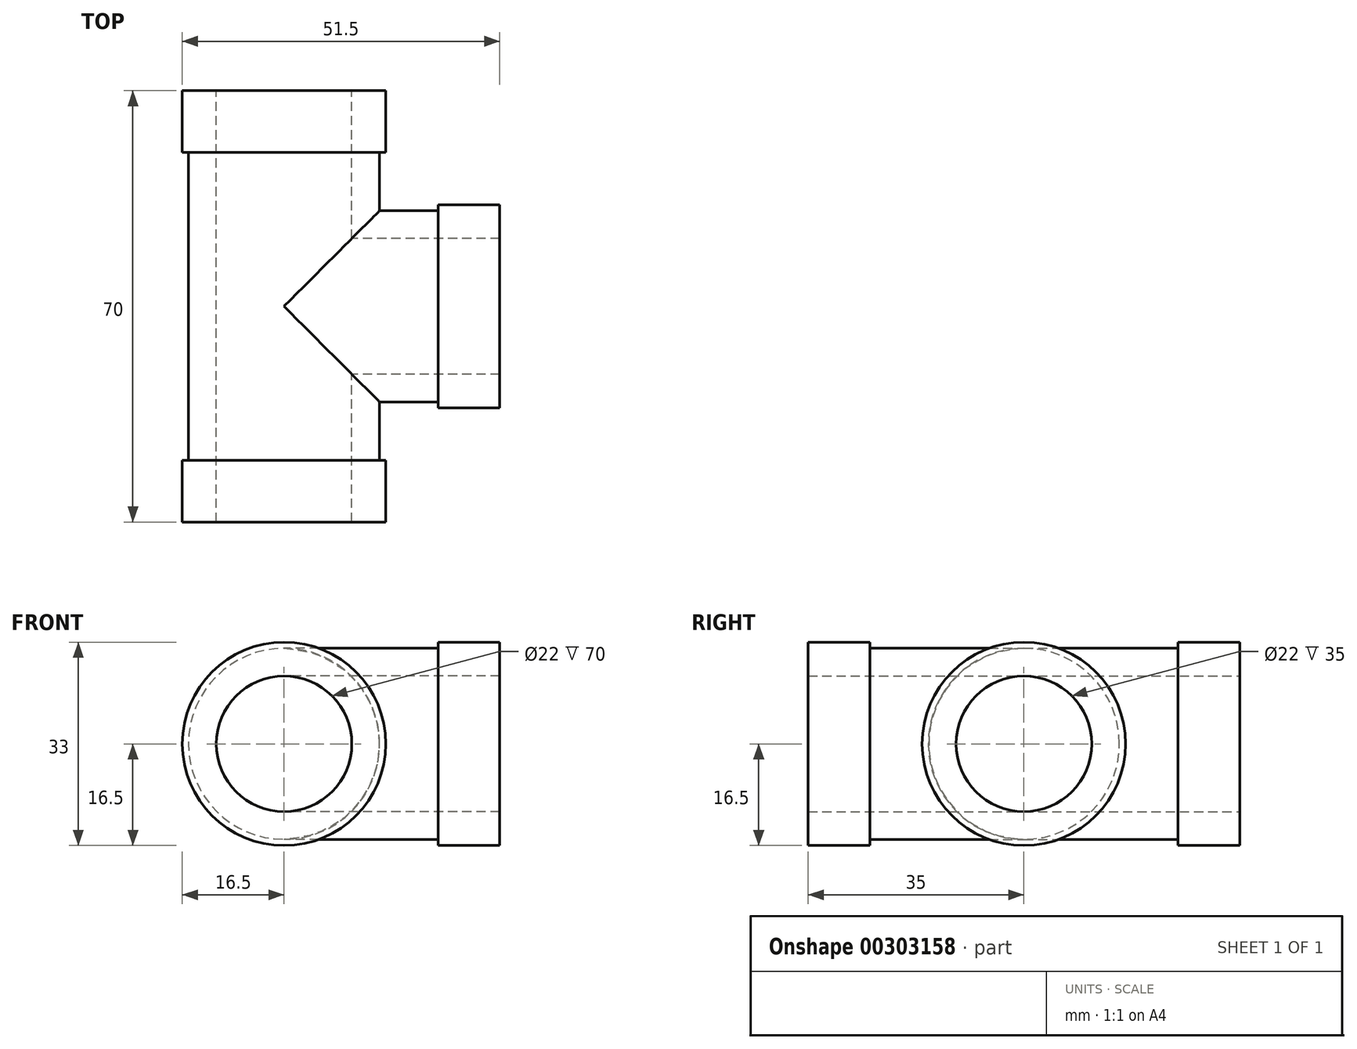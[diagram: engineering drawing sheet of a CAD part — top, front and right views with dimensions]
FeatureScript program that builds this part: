
annotation { "Feature Type Name" : "Feature", "Feature Type Description" : "" }
export const myFeature = defineFeature(function(context is Context, id is Id, definition is map)
    precondition{}
    {
        {
            var Q0;
            Q0=qCreatedBy(makeId("Front.planeOp"),FACE);
            var sketch = newSketch(context, id + "F0", { "sketchPlane" : qUnion([Q0])});
            skCircle(sketch, "E0", {"center": v(0, 0) * mm, "radius": 15.5 * mm});
            skCircle(sketch, "E1", {"center": v(0, 0) * mm, "radius": 11 * mm});
            skSolve(sketch);
        }
        {
            var Q0;
            Q0 = qSketchRegion(id + "F0", true);
            extrude(context, id + "F1", {"entities" : qUnion([Q0]), "depth" : 25 * mm});
        }
        {
            var Q0;
            Q0=makeQuery(id+"F1.opExtrude","CAP_FACE",FACE,{"disambiguationData":[OSD([sQuery(id+"F0.wireOp",EDGE,"E0"),sQuery(id+"F0.wireOp",EDGE,"E1")])],"isStart":false});
            var sketch = newSketch(context, id + "F2", { "sketchPlane" : qUnion([Q0])});
            skCircle(sketch, "E2", {"center": v(0, 0) * mm, "radius": 11 * mm});
            skCircle(sketch, "E3", {"center": v(0, 0) * mm, "radius": 16.5 * mm});
            skSolve(sketch);
        }
        {
            var Q0;
            Q0 = qSketchRegion(id + "F2", true);
            extrude(context, id + "F3", {"entities" : qUnion([Q0]), "operationType" : NewBodyOperationType.ADD, "depth" : 10 * mm});
        }
        {
            var Q0;
            Q0=makeQuery(id+"F1.opExtrude","SWEPT_BODY",BODY,{"disambiguationData":[OSD([sQuery(id+"F0.wireOp",EDGE,"E0"),sQuery(id+"F0.wireOp",EDGE,"E1")])]});
            var Q1;
            Q1=qCreatedBy(makeId("Front.planeOp"),FACE);
            mirror(context, id + "F4", {"operationType" : NewBodyOperationType.ADD, "entities" : qUnion([Q0]), "mirrorPlane" : qUnion([Q1])});
        }
        {
            var Q0;
            Q0=qCreatedBy(makeId("Right.planeOp"),FACE);
            var sketch = newSketch(context, id + "F5", { "sketchPlane" : qUnion([Q0])});
            skCircle(sketch, "E4", {"center": v(0, 0) * mm, "radius": 15.5 * mm});
            skCircle(sketch, "E5", {"center": v(0, 0) * mm, "radius": 11 * mm});
            skSolve(sketch);
        }
        {
            var Q0;
            Q0 = qSketchRegion(id + "F5", true);
            extrude(context, id + "F6", {"entities" : qUnion([Q0]), "operationType" : NewBodyOperationType.ADD, "depth" : 25 * mm});
        }
        {
            var Q0;
            Q0=makeQuery(id+"F6.opExtrude","CAP_FACE",FACE,{"disambiguationData":[OSD([sQuery(id+"F5.wireOp",EDGE,"E4"),sQuery(id+"F5.wireOp",EDGE,"E5")])],"isStart":false});
            var sketch = newSketch(context, id + "F7", { "sketchPlane" : qUnion([Q0])});
            skCircle(sketch, "E6", {"center": v(0, 0) * mm, "radius": 11 * mm});
            skCircle(sketch, "E7", {"center": v(0, 0) * mm, "radius": 16.5 * mm});
            skSolve(sketch);
        }
        {
            var Q0;
            Q0 = qSketchRegion(id + "F7", true);
            extrude(context, id + "F8", {"entities" : qUnion([Q0]), "operationType" : NewBodyOperationType.ADD, "depth" : 10 * mm});
        }
        {
            var Q0;
            Q0=makeQuery(id+"F3.opExtrude","CAP_FACE",FACE,{"disambiguationData":[OSD([sQuery(id+"F2.wireOp",EDGE,"E2"),sQuery(id+"F2.wireOp",EDGE,"E3")])],"isStart":false});
            var sketch = newSketch(context, id + "F9", { "sketchPlane" : qUnion([Q0])});
            skCircle(sketch, "E8", {"center": v(0, 0) * mm, "radius": 11 * mm});
            skSolve(sketch);
        }
        {
            var Q0;
            Q0 = qSketchRegion(id + "F9", true);
            extrude(context, id + "F10", {"entities" : qUnion([Q0]), "operationType" : NewBodyOperationType.REMOVE, "oppositeDirection" : true, "depth" : 200 * mm});
        }
        {
            var Q0;
            Q0=makeQuery(id+"F8.opExtrude","CAP_FACE",FACE,{"disambiguationData":[OSD([sQuery(id+"F7.wireOp",EDGE,"E6"),sQuery(id+"F7.wireOp",EDGE,"E7")])],"isStart":false});
            var sketch = newSketch(context, id + "F11", { "sketchPlane" : qUnion([Q0])});
            skCircle(sketch, "E9", {"center": v(0, 0) * mm, "radius": 11 * mm});
            skSolve(sketch);
        }
        {
            var Q0;
            Q0 = qSketchRegion(id + "F11", true);
            extrude(context, id + "F12", {"entities" : qUnion([Q0]), "operationType" : NewBodyOperationType.REMOVE, "oppositeDirection" : true, "depth" : 35 * mm});
        }
    });
